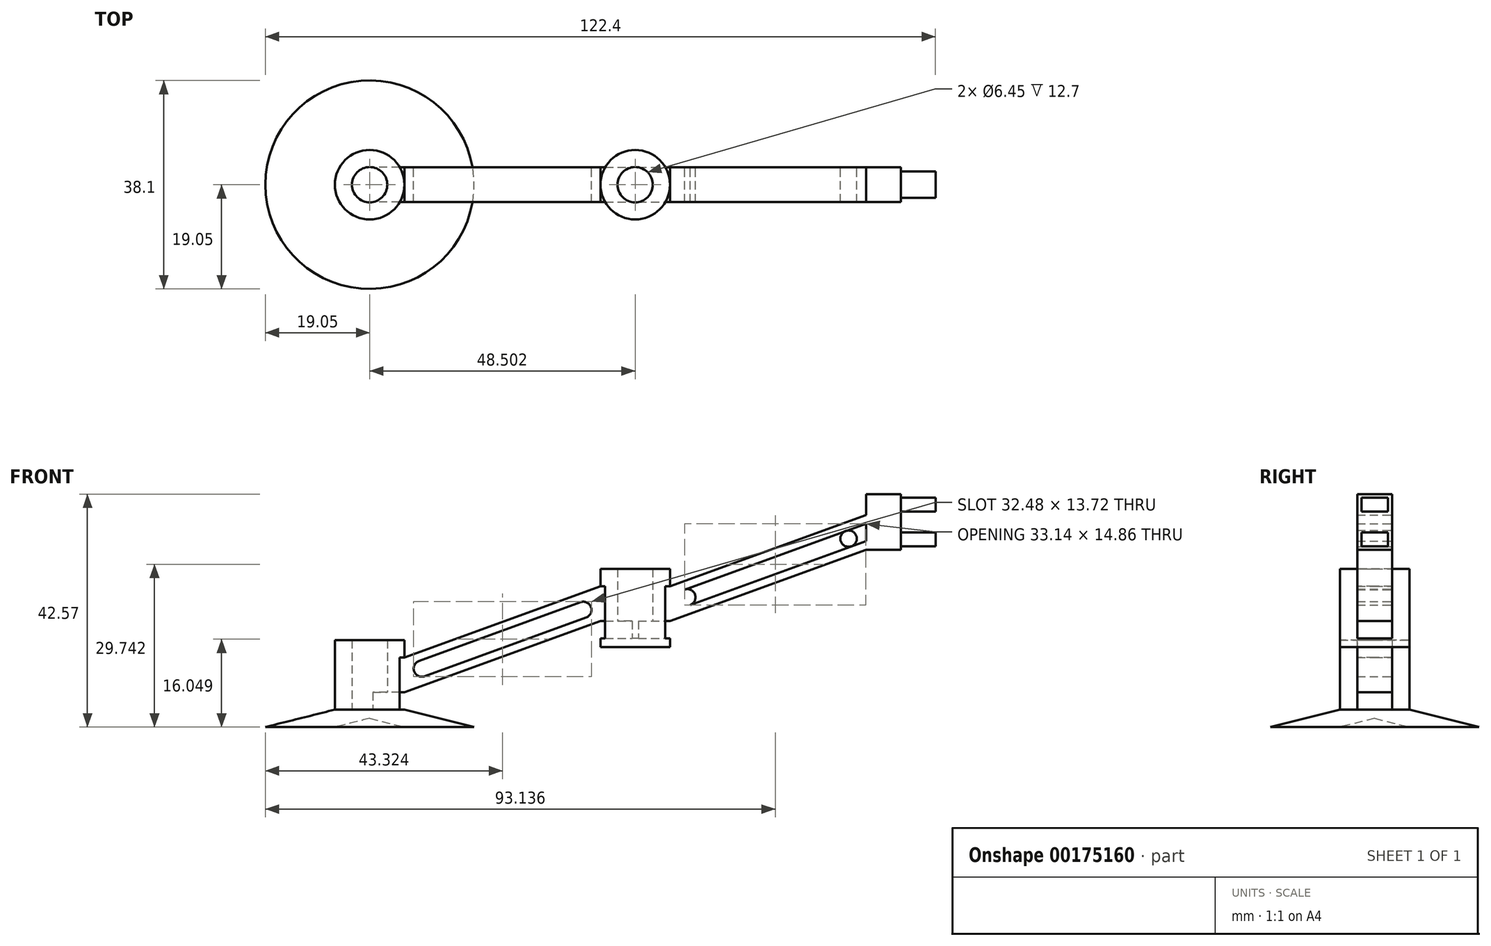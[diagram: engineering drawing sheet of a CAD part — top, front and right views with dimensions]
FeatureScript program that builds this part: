
annotation { "Feature Type Name" : "Feature", "Feature Type Description" : "" }
export const myFeature = defineFeature(function(context is Context, id is Id, definition is map)
    precondition{}
    {
        {
            var Q0;
            Q0=qCreatedBy(makeId("Front.planeOp"),FACE);
            var sketch = newSketch(context, id + "F0", { "sketchPlane" : qUnion([Q0])});
            skLineSegment(sketch, "E0.bottom", {"start": v(0, 3.18) * mm, "end": v(3.23, 3.18) * mm});
            skLineSegment(sketch, "E0.top", {"start": v(0, 15.88) * mm, "end": v(3.23, 15.88) * mm});
            skLineSegment(sketch, "E0.left", {"start": v(0, 3.17) * mm, "end": v(0, 15.88) * mm});
            skLineSegment(sketch, "E0.right", {"start": v(3.23, 3.18) * mm, "end": v(3.23, 15.88) * mm});
            skLineSegment(sketch, "E1.top", {"start": v(3.18, 15.88) * mm, "end": v(6.35, 15.88) * mm});
            skLineSegment(sketch, "E2", {"start": v(6.35, 0) * mm, "end": v(19.05, 0) * mm});
            skLineSegment(sketch, "E3", {"start": v(19.05, 0) * mm, "end": v(6.35, 3.18) * mm});
            skLineSegment(sketch, "E4", {"start": v(6.35, 15.88) * mm, "end": v(6.35, 3.18) * mm});
            skLineSegment(sketch, "E5", {"start": v(0, 3.17) * mm, "end": v(0, 1.59) * mm});
            skLineSegment(sketch, "E6", {"start": v(0, 1.59) * mm, "end": v(0, 0) * mm});
            skLineSegment(sketch, "E7", {"start": v(0, 1.59) * mm, "end": v(6.35, 0) * mm});
            skLineSegment(sketch, "E8.MirrorCS", {"start": v(0, 15.88) * mm, "end": v(-3.23, 15.88) * mm});
            skLineSegment(sketch, "E9.MirrorCS", {"start": v(-3.23, 3.17) * mm, "end": v(-3.23, 15.88) * mm});
            skLineSegment(sketch, "E10.MirrorCS", {"start": v(-3.18, 15.87) * mm, "end": v(-6.35, 15.87) * mm});
            skLineSegment(sketch, "E11.MirrorCS", {"start": v(-6.35, 15.88) * mm, "end": v(-6.35, 3.17) * mm});
            skLineSegment(sketch, "E12.MirrorCS", {"start": v(0, 3.18) * mm, "end": v(-3.23, 3.17) * mm});
            skLineSegment(sketch, "E13.MirrorCS", {"start": v(0, 1.59) * mm, "end": v(-6.35, 0) * mm});
            skLineSegment(sketch, "E14.MirrorCS", {"start": v(-6.35, 0) * mm, "end": v(-19.05, 0) * mm});
            skLineSegment(sketch, "E15.MirrorCS", {"start": v(-19.05, 0) * mm, "end": v(-6.35, 3.17) * mm});
            skPoint(sketch, "E16", {"position": v(6.35, 12.7) * mm});
            skPoint(sketch, "E17", {"position": v(6.35, 9.53) * mm});
            skPoint(sketch, "E18", {"position": v(6.35, 6.35) * mm});
            skLineSegment(sketch, "E19", {"start": v(6.35, 12.7) * mm, "end": v(42.15, 25.73) * mm});
            skLineSegment(sketch, "E20", {"start": v(6.35, 9.53) * mm, "end": v(42.1, 22.54) * mm});
            skLineSegment(sketch, "E21", {"start": v(6.35, 6.35) * mm, "end": v(42.15, 19.38) * mm});
            skLineSegment(sketch, "E22", {"start": v(42.15, 25.73) * mm, "end": v(42.15, 28.9) * mm});
            skLineSegment(sketch, "E23", {"start": v(42.15, 19.38) * mm, "end": v(42.15, 16.2) * mm});
            skLineSegment(sketch, "E24", {"start": v(42.15, 25.73) * mm, "end": v(42.15, 19.38) * mm});
            skLineSegment(sketch, "E25", {"start": v(42.15, 16.2) * mm, "end": v(54.85, 16.2) * mm});
            skLineSegment(sketch, "E26", {"start": v(54.85, 16.2) * mm, "end": v(54.85, 28.9) * mm});
            skLineSegment(sketch, "E27.bottom", {"start": v(48.5, 16.2) * mm, "end": v(45.28, 16.2) * mm});
            skLineSegment(sketch, "E27.top", {"start": v(48.5, 28.9) * mm, "end": v(45.28, 28.9) * mm});
            skLineSegment(sketch, "E27.left", {"start": v(48.5, 16.2) * mm, "end": v(48.5, 28.9) * mm});
            skLineSegment(sketch, "E27.right", {"start": v(45.28, 16.2) * mm, "end": v(45.28, 28.9) * mm});
            skLineSegment(sketch, "E28.MirrorCS", {"start": v(51.73, 16.2) * mm, "end": v(51.73, 28.9) * mm});
            skLineSegment(sketch, "E29.MirrorCS", {"start": v(48.5, 28.9) * mm, "end": v(51.73, 28.9) * mm});
            skLineSegment(sketch, "E30", {"start": v(42.15, 28.9) * mm, "end": v(45.28, 28.9) * mm});
            skLineSegment(sketch, "E31", {"start": v(51.73, 28.9) * mm, "end": v(54.85, 28.9) * mm});
            skLineSegment(sketch, "E32.top", {"start": v(42.15, 14.62) * mm, "end": v(54.85, 14.62) * mm});
            skLineSegment(sketch, "E32.left", {"start": v(42.15, 16.2) * mm, "end": v(42.15, 14.62) * mm});
            skLineSegment(sketch, "E32.right", {"start": v(54.85, 16.2) * mm, "end": v(54.85, 14.62) * mm});
            skLineSegment(sketch, "E33", {"start": v(54.85, 25.73) * mm, "end": v(90.65, 38.76) * mm});
            skLineSegment(sketch, "E34", {"start": v(54.85, 22.56) * mm, "end": v(90.65, 35.59) * mm});
            skLineSegment(sketch, "E35", {"start": v(54.85, 19.38) * mm, "end": v(90.65, 32.41) * mm});
            skLineSegment(sketch, "E36", {"start": v(90.65, 38.76) * mm, "end": v(90.65, 32.41) * mm});
            skLineSegment(sketch, "E37.bottom", {"start": v(90.65, 38.76) * mm, "end": v(97, 38.76) * mm});
            skLineSegment(sketch, "E37.top", {"start": v(90.65, 32.41) * mm, "end": v(97, 32.41) * mm});
            skLineSegment(sketch, "E37.right", {"start": v(97, 38.76) * mm, "end": v(97, 32.41) * mm});
            skLineSegment(sketch, "E38", {"start": v(48.5, 16.2) * mm, "end": v(48.5, 14.62) * mm});
            skLineSegment(sketch, "E39", {"start": v(6.35, 12.7) * mm, "end": v(3.23, 12.7) * mm});
            skLineSegment(sketch, "E40", {"start": v(6.35, 9.53) * mm, "end": v(3.23, 9.53) * mm});
            skLineSegment(sketch, "E41", {"start": v(6.35, 6.35) * mm, "end": v(3.23, 6.35) * mm});
            skLineSegment(sketch, "E42", {"start": v(42.15, 25.73) * mm, "end": v(45.28, 25.73) * mm});
            skLineSegment(sketch, "E43", {"start": v(42.1, 22.54) * mm, "end": v(45.28, 22.56) * mm});
            skLineSegment(sketch, "E44", {"start": v(42.15, 19.38) * mm, "end": v(45.28, 19.38) * mm});
            skLineSegment(sketch, "E45", {"start": v(54.85, 25.73) * mm, "end": v(51.73, 25.73) * mm});
            skLineSegment(sketch, "E46", {"start": v(54.85, 22.56) * mm, "end": v(51.73, 22.56) * mm});
            skLineSegment(sketch, "E47", {"start": v(54.85, 19.38) * mm, "end": v(51.73, 19.38) * mm});
            skPoint(sketch, "E48", {"position": v(6.35, 11.11) * mm});
            skPoint(sketch, "E49", {"position": v(6.35, 7.94) * mm});
            skPoint(sketch, "E50", {"position": v(42.15, 24.14) * mm});
            skPoint(sketch, "E51", {"position": v(42.15, 20.97) * mm});
            skLineSegment(sketch, "E52", {"start": v(6.35, 11.11) * mm, "end": v(42.15, 24.14) * mm});
            skLineSegment(sketch, "E53", {"start": v(42.15, 20.97) * mm, "end": v(6.35, 7.94) * mm});
            skPoint(sketch, "E54", {"position": v(40.51, 21.96) * mm});
            skLineSegment(sketch, "E55", {"start": v(40.51, 21.96) * mm, "end": v(39.02, 21.42) * mm});
            skCircle(sketch, "E56", {"center": v(39.02, 21.42) * mm, "radius": 1.5 * mm});
            skPoint(sketch, "E57", {"position": v(9.52, 10.68) * mm});
            skCircle(sketch, "E58", {"center": v(9.52, 10.68) * mm, "radius": 1.5 * mm});
            skLineSegment(sketch, "E59", {"start": v(48.5, 14.62) * mm, "end": v(48.5, 0) * mm});
            skLineSegment(sketch, "E60.bottom", {"start": v(54.85, 16.2) * mm, "end": v(55.1, 16.2) * mm});
            skLineSegment(sketch, "E60.top", {"start": v(54.85, 19.38) * mm, "end": v(55.1, 19.38) * mm});
            skLineSegment(sketch, "E60.left", {"start": v(54.85, 16.2) * mm, "end": v(54.85, 19.38) * mm});
            skLineSegment(sketch, "E60.right", {"start": v(55.1, 16.2) * mm, "end": v(55.1, 19.38) * mm});
            skPoint(sketch, "E61", {"position": v(54.85, 24.14) * mm});
            skPoint(sketch, "E62", {"position": v(54.85, 20.97) * mm});
            skPoint(sketch, "E63", {"position": v(90.65, 37.17) * mm});
            skPoint(sketch, "E64", {"position": v(90.65, 34) * mm});
            skLineSegment(sketch, "E65", {"start": v(54.85, 24.14) * mm, "end": v(90.65, 37.17) * mm});
            skLineSegment(sketch, "E66", {"start": v(90.65, 34) * mm, "end": v(54.85, 20.97) * mm});
            skPoint(sketch, "E67", {"position": v(58.03, 23.71) * mm});
            skPoint(sketch, "E68", {"position": v(87.48, 34.43) * mm});
            skCircle(sketch, "E69", {"center": v(87.48, 34.43) * mm, "radius": 1.5 * mm});
            skCircle(sketch, "E70", {"center": v(58.03, 23.71) * mm, "radius": 1.5 * mm});
            skLineSegment(sketch, "E71.top", {"start": v(90.65, 42.57) * mm, "end": v(97, 42.57) * mm});
            skLineSegment(sketch, "E71.left", {"start": v(90.65, 38.76) * mm, "end": v(90.65, 42.57) * mm});
            skLineSegment(sketch, "E71.right", {"start": v(97, 38.76) * mm, "end": v(97, 42.57) * mm});
            skSolve(sketch);
        }
        {
            var Q0;
            Q0=makeQuery(id+"F0.imprint","IMPRINT",FACE,{"disambiguationData":[TD([[makeQuery(id+"F0.imprint","IMPRINT",EDGE,{"derivedFrom":sQuery(id+"F0.wireOp",EDGE,"E0.bottom")}),-1.0]])]});
            var Q1;
            {var subQ0=sQuery(id+"F0.wireOp",EDGE,"E40");Q1=makeQuery(id+"F0.imprint","IMPRINT",FACE,{"disambiguationData":[TD([[makeQuery(id+"F0.imprint","IMPRINT",EDGE,{"derivedFrom":subQ0}),1.0]])]});}
            var Q2;
            {var subQ0=sQuery(id+"F0.wireOp",EDGE,"E39");Q2=makeQuery(id+"F0.imprint","IMPRINT",FACE,{"disambiguationData":[TD([[makeQuery(id+"F0.imprint","IMPRINT",EDGE,{"derivedFrom":subQ0}),1.0]])]});}
            var Q3;
            {var subQ0=sQuery(id+"F0.wireOp",EDGE,"E1.top");Q3=makeQuery(id+"F0.imprint","IMPRINT",FACE,{"disambiguationData":[TD([[makeQuery(id+"F0.imprint","IMPRINT",EDGE,{"derivedFrom":subQ0}),-1.0]])]});}
            var Q4;
            Q4=sQuery(id+"F0.wireOp",EDGE,"E0.left");
            revolve(context, id + "F1", {"entities" : qUnion([Q0, Q1, Q2, Q3]), "axis" : qUnion([Q4]), "revolveType" : RevolveType.FULL});
        }
        {
            var Q0;
            {var subQ4=sQuery(id+"F0.wireOp",EDGE,"E21");Q0=makeQuery(id+"F0.imprint","IMPRINT",FACE,{"disambiguationData":[TD([[makeQuery(id+"F0.imprint","IMPRINT",EDGE,{"derivedFrom":subQ4}),1.0]])]});}
            var Q1;
            {var subQ1=sQuery(id+"F0.wireOp",EDGE,"E4");var subQ3=sQuery(id+"F0.wireOp",EDGE,"E53");var subQ4=makeQuery(id+"F0.imprint","INTERSECT",VERTEX,{"derivedFrom":[subQ1,subQ3]});Q1=makeQuery(id+"F0.imprint","IMPRINT",FACE,{"disambiguationData":[TD([[makeQuery(id+"F0.imprint","IMPRINT",EDGE,{"disambiguationData":[TD([[subQ4,1.0]])],"derivedFrom":subQ3}),-1.0]])]});}
            var Q2;
            {var subQ1=sQuery(id+"F0.wireOp",EDGE,"E4");var subQ3=sQuery(id+"F0.wireOp",EDGE,"E52");var subQ4=makeQuery(id+"F0.imprint","INTERSECT",VERTEX,{"derivedFrom":[subQ1,subQ3]});Q2=makeQuery(id+"F0.imprint","IMPRINT",FACE,{"disambiguationData":[TD([[makeQuery(id+"F0.imprint","IMPRINT",EDGE,{"disambiguationData":[TD([[subQ4,-1.0]])],"derivedFrom":subQ3}),-1.0]])]});}
            var Q3;
            {var subQ6=sQuery(id+"F0.wireOp",EDGE,"E19");Q3=makeQuery(id+"F0.imprint","IMPRINT",FACE,{"disambiguationData":[TD([[makeQuery(id+"F0.imprint","IMPRINT",EDGE,{"derivedFrom":subQ6}),-1.0]])]});}
            var Q4;
            {var subQ0=sQuery(id+"F0.wireOp",EDGE,"E39");Q4=makeQuery(id+"F0.imprint","IMPRINT",FACE,{"disambiguationData":[TD([[makeQuery(id+"F0.imprint","IMPRINT",EDGE,{"derivedFrom":subQ0}),1.0]])]});}
            var Q5;
            {var subQ0=sQuery(id+"F0.wireOp",EDGE,"E40");Q5=makeQuery(id+"F0.imprint","IMPRINT",FACE,{"disambiguationData":[TD([[makeQuery(id+"F0.imprint","IMPRINT",EDGE,{"derivedFrom":subQ0}),1.0]])]});}
            var Q6;
            {var subQ5=sQuery(id+"F0.wireOp",EDGE,"E52");var subQ6=sQuery(id+"F0.wireOp",EDGE,"E24");var subQ7=makeQuery(id+"F0.imprint","INTERSECT",VERTEX,{"derivedFrom":[subQ6,subQ5]});Q6=makeQuery(id+"F0.imprint","IMPRINT",FACE,{"disambiguationData":[TD([[makeQuery(id+"F0.imprint","IMPRINT",EDGE,{"disambiguationData":[TD([[subQ7,1.0]])],"derivedFrom":subQ5}),-1.0]])]});}
            var Q7;
            {var subQ5=sQuery(id+"F0.wireOp",EDGE,"E53");var subQ6=sQuery(id+"F0.wireOp",EDGE,"E24");var subQ7=makeQuery(id+"F0.imprint","INTERSECT",VERTEX,{"derivedFrom":[subQ6,subQ5]});Q7=makeQuery(id+"F0.imprint","IMPRINT",FACE,{"disambiguationData":[TD([[makeQuery(id+"F0.imprint","IMPRINT",EDGE,{"disambiguationData":[TD([[subQ7,-1.0]])],"derivedFrom":subQ5}),-1.0]])]});}
            var Q8;
            {var subQ0=sQuery(id+"F0.wireOp",EDGE,"E42");Q8=makeQuery(id+"F0.imprint","IMPRINT",FACE,{"disambiguationData":[TD([[makeQuery(id+"F0.imprint","IMPRINT",EDGE,{"derivedFrom":subQ0}),-1.0]])]});}
            var Q9;
            {var subQ0=sQuery(id+"F0.wireOp",EDGE,"E43");Q9=makeQuery(id+"F0.imprint","IMPRINT",FACE,{"disambiguationData":[TD([[makeQuery(id+"F0.imprint","IMPRINT",EDGE,{"derivedFrom":subQ0}),-1.0]])]});}
            var Q10;
            Q10=makeQuery(id+"F0.imprint","IMPRINT",FACE,{"disambiguationData":[TD([[makeQuery(id+"F0.imprint","IMPRINT",EDGE,{"derivedFrom":sQuery(id+"F0.wireOp",EDGE,"E60.bottom")}),1.0]])]});
            var Q11;
            {var subQ0=sQuery(id+"F0.wireOp",EDGE,"E46");Q11=makeQuery(id+"F0.imprint","IMPRINT",FACE,{"disambiguationData":[TD([[makeQuery(id+"F0.imprint","IMPRINT",EDGE,{"derivedFrom":subQ0}),1.0]])]});}
            var Q12;
            {var subQ0=sQuery(id+"F0.wireOp",EDGE,"E45");Q12=makeQuery(id+"F0.imprint","IMPRINT",FACE,{"disambiguationData":[TD([[makeQuery(id+"F0.imprint","IMPRINT",EDGE,{"derivedFrom":subQ0}),1.0]])]});}
            var Q13;
            {var subQ1=sQuery(id+"F0.wireOp",EDGE,"E33");Q13=makeQuery(id+"F0.imprint","IMPRINT",FACE,{"disambiguationData":[TD([[makeQuery(id+"F0.imprint","IMPRINT",EDGE,{"derivedFrom":subQ1}),-1.0]])]});}
            var Q14;
            {var subQ1=sQuery(id+"F0.wireOp",EDGE,"E26");var subQ3=sQuery(id+"F0.wireOp",EDGE,"E65");var subQ4=makeQuery(id+"F0.imprint","INTERSECT",VERTEX,{"derivedFrom":[subQ1,subQ3]});Q14=makeQuery(id+"F0.imprint","IMPRINT",FACE,{"disambiguationData":[TD([[makeQuery(id+"F0.imprint","IMPRINT",EDGE,{"disambiguationData":[TD([[subQ4,-1.0]])],"derivedFrom":subQ3}),-1.0]])]});}
            var Q15;
            {var subQ1=sQuery(id+"F0.wireOp",EDGE,"E26");var subQ3=sQuery(id+"F0.wireOp",EDGE,"E66");var subQ4=makeQuery(id+"F0.imprint","INTERSECT",VERTEX,{"derivedFrom":[subQ1,subQ3]});Q15=makeQuery(id+"F0.imprint","IMPRINT",FACE,{"disambiguationData":[TD([[makeQuery(id+"F0.imprint","IMPRINT",EDGE,{"disambiguationData":[TD([[subQ4,1.0]])],"derivedFrom":subQ3}),-1.0]])]});}
            var Q16;
            {var subQ4=sQuery(id+"F0.wireOp",EDGE,"E35");Q16=makeQuery(id+"F0.imprint","IMPRINT",FACE,{"disambiguationData":[TD([[makeQuery(id+"F0.imprint","IMPRINT",EDGE,{"derivedFrom":subQ4}),1.0]])]});}
            var Q17;
            {var subQ0=sQuery(id+"F0.wireOp",EDGE,"E36");var subQ1=sQuery(id+"F0.wireOp",EDGE,"E34");var subQ2=makeQuery(id+"F0.imprint","INTERSECT",VERTEX,{"derivedFrom":[subQ1,subQ0]});Q17=makeQuery(id+"F0.imprint","IMPRINT",FACE,{"disambiguationData":[TD([[makeQuery(id+"F0.imprint","IMPRINT",EDGE,{"disambiguationData":[TD([[subQ2,1.0]])],"derivedFrom":subQ1}),-1.0]])]});}
            var Q18;
            {var subQ0=sQuery(id+"F0.wireOp",EDGE,"E36");var subQ1=sQuery(id+"F0.wireOp",EDGE,"E34");var subQ2=makeQuery(id+"F0.imprint","INTERSECT",VERTEX,{"derivedFrom":[subQ1,subQ0]});Q18=makeQuery(id+"F0.imprint","IMPRINT",FACE,{"disambiguationData":[TD([[makeQuery(id+"F0.imprint","IMPRINT",EDGE,{"disambiguationData":[TD([[subQ2,1.0]])],"derivedFrom":subQ1}),1.0]])]});}
            var Q19;
            {var subQ3=sQuery(id+"F0.wireOp",EDGE,"E37.bottom");Q19=makeQuery(id+"F0.imprint","IMPRINT",FACE,{"disambiguationData":[TD([[makeQuery(id+"F0.imprint","IMPRINT",EDGE,{"derivedFrom":subQ3}),-1.0]])]});}
            var Q20;
            {var subQ5=sQuery(id+"F0.wireOp",EDGE,"E37.top");Q20=makeQuery(id+"F0.imprint","IMPRINT",FACE,{"disambiguationData":[TD([[makeQuery(id+"F0.imprint","IMPRINT",EDGE,{"derivedFrom":subQ5}),1.0]])]});}
            var Q21;
            Q21=makeQuery(id+"F0.imprint","IMPRINT",FACE,{"disambiguationData":[TD([[makeQuery(id+"F0.imprint","IMPRINT",EDGE,{"derivedFrom":sQuery(id+"F0.wireOp",EDGE,"E37.bottom")}),1.0]])]});
            extrude(context, id + "F2", {"entities" : qUnion([Q0, Q1, Q2, Q3, Q4, Q5, Q6, Q7, Q8, Q9, Q10, Q11, Q12, Q13, Q14, Q15, Q16, Q17, Q18, Q19, Q20, Q21]), "operationType" : NewBodyOperationType.ADD, "endBound" : BoundingType.SYMMETRIC, "depth" : 6.35 * mm});
        }
        {
            var Q0;
            {var subQ0=sQuery(id+"F0.wireOp",EDGE,"E32.left");Q0=makeQuery(id+"F0.imprint","IMPRINT",FACE,{"disambiguationData":[TD([[makeQuery(id+"F0.imprint","IMPRINT",EDGE,{"derivedFrom":subQ0}),1.0]])]});}
            var Q1;
            {var subQ0=sQuery(id+"F0.wireOp",EDGE,"E23");Q1=makeQuery(id+"F0.imprint","IMPRINT",FACE,{"disambiguationData":[TD([[makeQuery(id+"F0.imprint","IMPRINT",EDGE,{"derivedFrom":subQ0}),1.0]])]});}
            var Q2;
            {var subQ0=sQuery(id+"F0.wireOp",EDGE,"E43");Q2=makeQuery(id+"F0.imprint","IMPRINT",FACE,{"disambiguationData":[TD([[makeQuery(id+"F0.imprint","IMPRINT",EDGE,{"derivedFrom":subQ0}),-1.0]])]});}
            var Q3;
            {var subQ0=sQuery(id+"F0.wireOp",EDGE,"E42");Q3=makeQuery(id+"F0.imprint","IMPRINT",FACE,{"disambiguationData":[TD([[makeQuery(id+"F0.imprint","IMPRINT",EDGE,{"derivedFrom":subQ0}),-1.0]])]});}
            var Q4;
            Q4=makeQuery(id+"F0.imprint","IMPRINT",FACE,{"disambiguationData":[TD([[makeQuery(id+"F0.imprint","IMPRINT",EDGE,{"derivedFrom":sQuery(id+"F0.wireOp",EDGE,"E22")}),-1.0]])]});
            var Q5;
            Q5=sQuery(id+"F0.wireOp",EDGE,"E27.left");
            revolve(context, id + "F3", {"operationType" : NewBodyOperationType.ADD, "entities" : qUnion([Q0, Q1, Q2, Q3, Q4]), "axis" : qUnion([Q5]), "revolveType" : RevolveType.FULL});
        }
        {
            var Q0;
            Q0=qCreatedBy(makeId("Right.planeOp"),FACE);
            var sketch = newSketch(context, id + "F4", { "sketchPlane" : qUnion([Q0])});
            skLineSegment(sketch, "E72", {"start": v(0, 0) * mm, "end": v(0, 3.17) * mm});
            skLineSegment(sketch, "E73.bottom", {"start": v(0, 3.17) * mm, "end": v(-3.17, 3.17) * mm});
            skLineSegment(sketch, "E73.top", {"start": v(0, 6.35) * mm, "end": v(-3.18, 6.35) * mm});
            skLineSegment(sketch, "E73.left", {"start": v(0, 3.17) * mm, "end": v(0, 6.35) * mm});
            skLineSegment(sketch, "E73.right", {"start": v(-3.17, 3.17) * mm, "end": v(-3.18, 6.35) * mm});
            skLineSegment(sketch, "E74.MirrorCS", {"start": v(0, 6.35) * mm, "end": v(3.18, 6.35) * mm});
            skLineSegment(sketch, "E75.MirrorCS", {"start": v(3.17, 3.17) * mm, "end": v(3.18, 6.35) * mm});
            skLineSegment(sketch, "E76.MirrorCS", {"start": v(0, 3.17) * mm, "end": v(3.17, 3.17) * mm});
            skLineSegment(sketch, "E77", {"start": v(0, 0) * mm, "end": v(0, 14.62) * mm});
            skSolve(sketch);
        }
        {
            var Q0;
            Q0 = qSketchRegion(id + "F4", true);
            extrude(context, id + "F5", {"entities" : qUnion([Q0]), "operationType" : NewBodyOperationType.REMOVE, "depth" : 6.35 * mm});
        }
        {
            var Q0;
            Q0=makeQuery(id+"F2.opExtrude","SWEPT_FACE",FACE,{"disambiguationData":[OSD([sQuery(id+"F0.wireOp",EDGE,"E60.right")])]});
            var sketch = newSketch(context, id + "F6", { "sketchPlane" : qUnion([Q0])});
            skLineSegment(sketch, "E78.bottom", {"start": v(-3.18, 19.38) * mm, "end": v(3.18, 19.38) * mm});
            skLineSegment(sketch, "E78.top", {"start": v(-3.18, 16.2) * mm, "end": v(3.18, 16.2) * mm});
            skLineSegment(sketch, "E78.left", {"start": v(-3.18, 19.38) * mm, "end": v(-3.18, 16.2) * mm});
            skLineSegment(sketch, "E78.right", {"start": v(3.18, 19.38) * mm, "end": v(3.18, 16.2) * mm});
            skSolve(sketch);
        }
        {
            var Q0;
            Q0 = qSketchRegion(id + "F6", true);
            extrude(context, id + "F7", {"entities" : qUnion([Q0]), "operationType" : NewBodyOperationType.REMOVE, "oppositeDirection" : true, "depth" : 12.95 * mm});
        }
        {
            var Q0;
            Q0=makeQuery(id+"F2.opExtrude","SWEPT_FACE",FACE,{"disambiguationData":[OSD([sQuery(id+"F0.wireOp",EDGE,"E37.right")])]});
            var sketch = newSketch(context, id + "F8", { "sketchPlane" : qUnion([Q0])});
            skPoint(sketch, "E79", {"position": v(0, 37.5) * mm});
            skPoint(sketch, "E79.positionSnap0", {"position": v(0, 32.41) * mm});
            skPoint(sketch, "E79.positionSnap1", {"position": v(3.17, 37.5) * mm});
            skLineSegment(sketch, "E80.bottom", {"start": v(-2.4, 41.94) * mm, "end": v(2.4, 41.94) * mm});
            skLineSegment(sketch, "E80.top", {"start": v(-2.4, 33.05) * mm, "end": v(2.4, 33.05) * mm});
            skLineSegment(sketch, "E81", {"start": v(-2.4, 39.4) * mm, "end": v(2.4, 39.4) * mm});
            skLineSegment(sketch, "E82", {"start": v(-2.4, 35.59) * mm, "end": v(2.4, 35.59) * mm});
            skLineSegment(sketch, "E83", {"start": v(-2.4, 41.94) * mm, "end": v(-2.4, 39.4) * mm});
            skLineSegment(sketch, "E84", {"start": v(2.4, 41.94) * mm, "end": v(2.4, 39.4) * mm});
            skLineSegment(sketch, "E85", {"start": v(2.4, 35.59) * mm, "end": v(2.4, 33.05) * mm});
            skLineSegment(sketch, "E86", {"start": v(-2.4, 35.59) * mm, "end": v(-2.4, 33.05) * mm});
            skLineSegment(sketch, "E87", {"start": v(0, 37.5) * mm, "end": v(0, 42.57) * mm});
            skLineSegment(sketch, "E88", {"start": v(0, 42.57) * mm, "end": v(0, 37.5) * mm});
            skLineSegment(sketch, "E89", {"start": v(0, 37.5) * mm, "end": v(0, 32.41) * mm});
            skLineSegment(sketch, "E90", {"start": v(2.4, 41.94) * mm, "end": v(-2.4, 39.4) * mm});
            skLineSegment(sketch, "E91", {"start": v(-2.4, 41.94) * mm, "end": v(2.4, 39.4) * mm});
            skLineSegment(sketch, "E92", {"start": v(2.4, 35.59) * mm, "end": v(-2.4, 33.05) * mm});
            skLineSegment(sketch, "E93", {"start": v(-2.4, 35.59) * mm, "end": v(2.4, 33.05) * mm});
            skPoint(sketch, "E94", {"position": v(0, 40.67) * mm});
            skPoint(sketch, "E95", {"position": v(0, 34.32) * mm});
            skSolve(sketch);
        }
        {
            var Q0;
            Q0=makeQuery(id+"F8.imprint","IMPRINT",FACE,{"disambiguationData":[TD([[makeQuery(id+"F8.imprint","IMPRINT",EDGE,{"derivedFrom":sQuery(id+"F8.wireOp",EDGE,"E80.bottom")}),-1.0]])]});
            var Q1;
            Q1=makeQuery(id+"F8.imprint","IMPRINT",FACE,{"disambiguationData":[TD([[makeQuery(id+"F8.imprint","IMPRINT",EDGE,{"derivedFrom":sQuery(id+"F8.wireOp",EDGE,"E80.top")}),1.0]])]});
            var Q2;
            {var subQ0=sQuery(id+"F8.wireOp",EDGE,"E85");Q2=makeQuery(id+"F8.imprint","IMPRINT",FACE,{"disambiguationData":[TD([[makeQuery(id+"F8.imprint","IMPRINT",EDGE,{"derivedFrom":subQ0}),-1.0]])]});}
            var Q3;
            {var subQ1=sQuery(id+"F8.wireOp",EDGE,"E82");var subQ3=sQuery(id+"F8.wireOp",EDGE,"E89");var subQ4=makeQuery(id+"F8.imprint","INTERSECT",VERTEX,{"derivedFrom":[subQ1,subQ3]});Q3=makeQuery(id+"F8.imprint","IMPRINT",FACE,{"disambiguationData":[TD([[makeQuery(id+"F8.imprint","IMPRINT",EDGE,{"disambiguationData":[TD([[subQ4,-1.0]])],"derivedFrom":subQ1}),-1.0]])]});}
            var Q4;
            {var subQ1=sQuery(id+"F8.wireOp",EDGE,"E82");var subQ3=sQuery(id+"F8.wireOp",EDGE,"E89");var subQ4=makeQuery(id+"F8.imprint","INTERSECT",VERTEX,{"derivedFrom":[subQ1,subQ3]});Q4=makeQuery(id+"F8.imprint","IMPRINT",FACE,{"disambiguationData":[TD([[makeQuery(id+"F8.imprint","IMPRINT",EDGE,{"disambiguationData":[TD([[subQ4,1.0]])],"derivedFrom":subQ1}),-1.0]])]});}
            var Q5;
            {var subQ0=sQuery(id+"F8.wireOp",EDGE,"E86");Q5=makeQuery(id+"F8.imprint","IMPRINT",FACE,{"disambiguationData":[TD([[makeQuery(id+"F8.imprint","IMPRINT",EDGE,{"derivedFrom":subQ0}),1.0]])]});}
            var Q6;
            {var subQ1=sQuery(id+"F8.wireOp",EDGE,"E81");var subQ3=sQuery(id+"F8.wireOp",EDGE,"E88");var subQ4=makeQuery(id+"F8.imprint","INTERSECT",VERTEX,{"derivedFrom":[subQ1,subQ3]});Q6=makeQuery(id+"F8.imprint","IMPRINT",FACE,{"disambiguationData":[TD([[makeQuery(id+"F8.imprint","IMPRINT",EDGE,{"disambiguationData":[TD([[subQ4,1.0]])],"derivedFrom":subQ1}),1.0]])]});}
            var Q7;
            {var subQ0=sQuery(id+"F8.wireOp",EDGE,"E83");Q7=makeQuery(id+"F8.imprint","IMPRINT",FACE,{"disambiguationData":[TD([[makeQuery(id+"F8.imprint","IMPRINT",EDGE,{"derivedFrom":subQ0}),1.0]])]});}
            var Q8;
            {var subQ1=sQuery(id+"F8.wireOp",EDGE,"E81");var subQ3=sQuery(id+"F8.wireOp",EDGE,"E88");var subQ4=makeQuery(id+"F8.imprint","INTERSECT",VERTEX,{"derivedFrom":[subQ1,subQ3]});Q8=makeQuery(id+"F8.imprint","IMPRINT",FACE,{"disambiguationData":[TD([[makeQuery(id+"F8.imprint","IMPRINT",EDGE,{"disambiguationData":[TD([[subQ4,-1.0]])],"derivedFrom":subQ1}),1.0]])]});}
            var Q9;
            {var subQ0=sQuery(id+"F8.wireOp",EDGE,"E84");Q9=makeQuery(id+"F8.imprint","IMPRINT",FACE,{"disambiguationData":[TD([[makeQuery(id+"F8.imprint","IMPRINT",EDGE,{"derivedFrom":subQ0}),-1.0]])]});}
            extrude(context, id + "F9", {"entities" : qUnion([Q0, Q1, Q2, Q3, Q4, Q5, Q6, Q7, Q8, Q9]), "operationType" : NewBodyOperationType.ADD, "depth" : 6.35 * mm});
        }
    });
